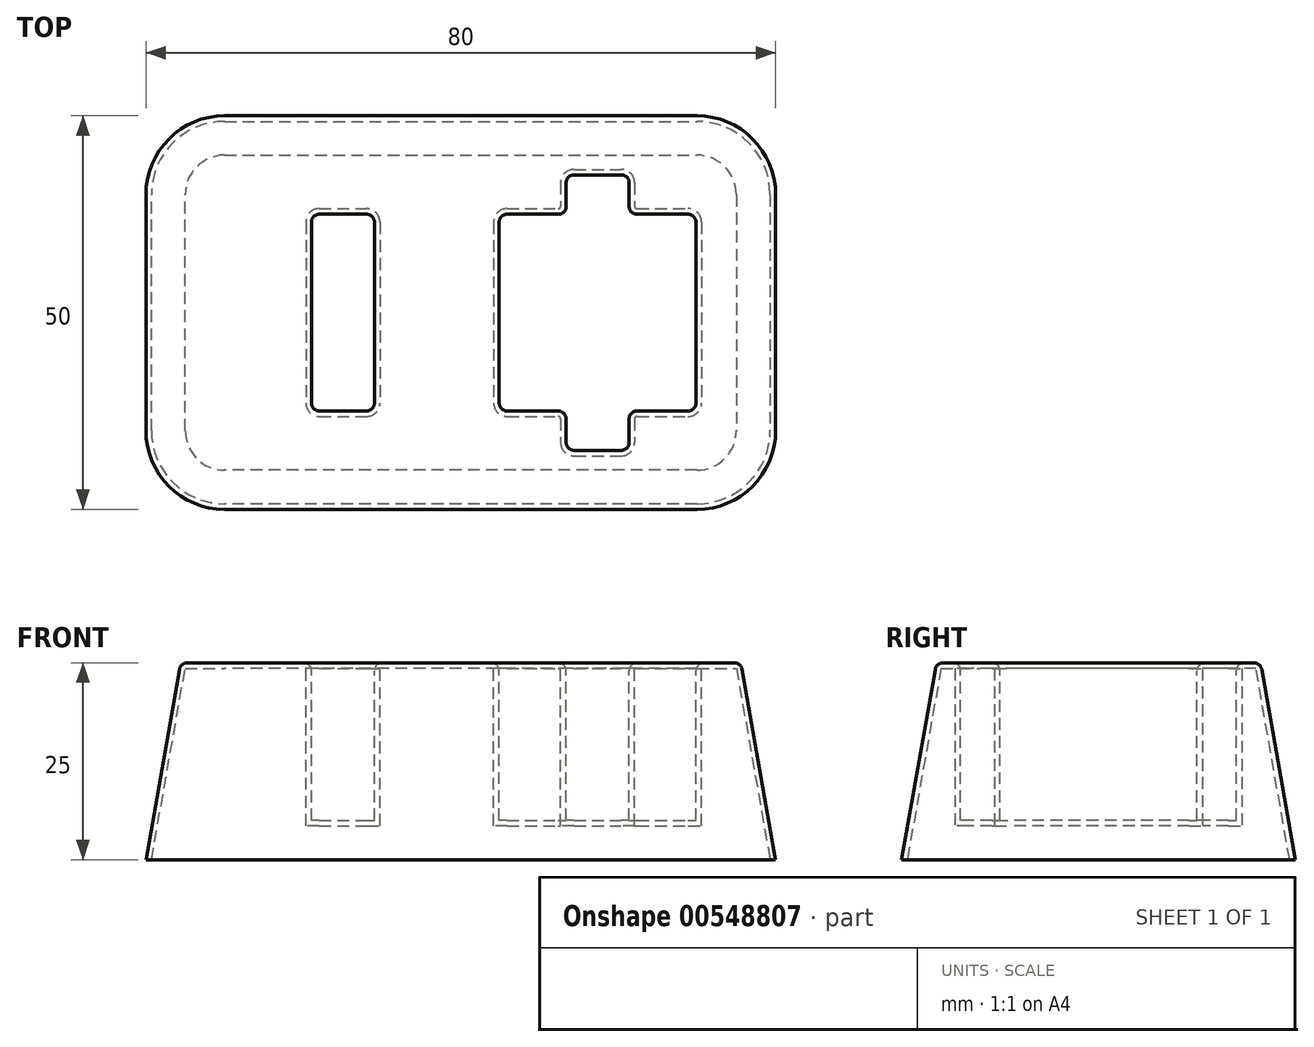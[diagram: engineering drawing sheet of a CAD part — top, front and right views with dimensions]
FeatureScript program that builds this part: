
annotation { "Feature Type Name" : "Feature", "Feature Type Description" : "" }
export const myFeature = defineFeature(function(context is Context, id is Id, definition is map)
    precondition{}
    {
        {
            var Q0;
            Q0=qCreatedBy(makeId("Top.planeOp"),FACE);
            var sketch = newSketch(context, id + "F0", { "sketchPlane" : qUnion([Q0])});
            skLineSegment(sketch, "E0.bottom", {"start": v(30, 25) * mm, "end": v(-30, 25) * mm});
            skLineSegment(sketch, "E0.top", {"start": v(30, -25) * mm, "end": v(-30, -25) * mm});
            skLineSegment(sketch, "E0.left", {"start": v(40, 15) * mm, "end": v(40, -15) * mm});
            skLineSegment(sketch, "E0.right", {"start": v(-40, 15) * mm, "end": v(-40, -15) * mm});
            skPoint(sketch, "E0.middle", {"position": v(0, 0) * mm});
            skPoint(sketch, "E1.visualSharp", {"position": v(-40, 25) * mm});
            skArc(sketch, "E1.filletArc", {"start": v(-30, 25) * mm, "mid": v(-37.07, 22.07) * mm, "end": v(-40, 15) * mm});
            skPoint(sketch, "E2.visualSharp", {"position": v(40, 25) * mm});
            skArc(sketch, "E2.filletArc", {"start": v(40, 15) * mm, "mid": v(37.07, 22.07) * mm, "end": v(30, 25) * mm});
            skPoint(sketch, "E3.visualSharp", {"position": v(40, -25) * mm});
            skArc(sketch, "E3.filletArc", {"start": v(30, -25) * mm, "mid": v(37.07, -22.07) * mm, "end": v(40, -15) * mm});
            skPoint(sketch, "E4.visualSharp", {"position": v(-40, -25) * mm});
            skArc(sketch, "E4.filletArc", {"start": v(-40, -15) * mm, "mid": v(-37.07, -22.07) * mm, "end": v(-30, -25) * mm});
            skSolve(sketch);
        }
        {
            var Q0;
            Q0 = qSketchRegion(id + "F0", true);
            extrude(context, id + "F1", {"entities" : qUnion([Q0]), "depth" : 25 * mm, "offsetDistance" : 25 * mm, "hasDraft" : true, "draftAngle" : 10 * degree, "draftPullDirection" : true});
        }
        {
            var Q0;
            Q0=makeQuery(id+"F1.opExtrude","CAP_FACE",FACE,{"disambiguationData":[OSD([sQuery(id+"F0.wireOp",EDGE,"E0.bottom"),sQuery(id+"F0.wireOp",EDGE,"E0.top"),sQuery(id+"F0.wireOp",EDGE,"E0.left"),sQuery(id+"F0.wireOp",EDGE,"E0.right"),sQuery(id+"F0.wireOp",EDGE,"E1.filletArc"),sQuery(id+"F0.wireOp",EDGE,"E2.filletArc"),sQuery(id+"F0.wireOp",EDGE,"E3.filletArc"),sQuery(id+"F0.wireOp",EDGE,"E4.filletArc")])],"isStart":false});
            var sketch = newSketch(context, id + "F2", { "sketchPlane" : qUnion([Q0])});
            skLineSegment(sketch, "E5.bottom", {"start": v(14.38, 17.5) * mm, "end": v(20.38, 17.5) * mm});
            skLineSegment(sketch, "E5.top", {"start": v(14.38, -17.5) * mm, "end": v(20.38, -17.5) * mm});
            skLineSegment(sketch, "E5.left", {"start": v(13.38, 16.5) * mm, "end": v(13.38, 13.5) * mm});
            skLineSegment(sketch, "E5.right", {"start": v(21.38, 16.5) * mm, "end": v(21.38, 13.5) * mm});
            skPoint(sketch, "E5.middle", {"position": v(17.38, 0) * mm});
            skLineSegment(sketch, "E6.bottom", {"start": v(5.88, 12.5) * mm, "end": v(12.38, 12.5) * mm});
            skLineSegment(sketch, "E6.top", {"start": v(5.88, -12.5) * mm, "end": v(12.38, -12.5) * mm});
            skLineSegment(sketch, "E6.left", {"start": v(4.88, 11.5) * mm, "end": v(4.88, -11.5) * mm});
            skLineSegment(sketch, "E6.right", {"start": v(29.88, 11.5) * mm, "end": v(29.88, -11.5) * mm});
            skLineSegment(sketch, "E7.trimOffspring", {"start": v(22.38, 12.5) * mm, "end": v(28.88, 12.5) * mm});
            skLineSegment(sketch, "E8.trimOffspring", {"start": v(13.38, -13.5) * mm, "end": v(13.38, -16.5) * mm});
            skLineSegment(sketch, "E9.trimOffspring", {"start": v(21.38, -13.5) * mm, "end": v(21.38, -16.5) * mm});
            skLineSegment(sketch, "E10.trimOffspring", {"start": v(22.38, -12.5) * mm, "end": v(28.88, -12.5) * mm});
            skPoint(sketch, "E11.visualSharp", {"position": v(13.38, 17.5) * mm});
            skArc(sketch, "E11.filletArc", {"start": v(14.38, 17.5) * mm, "mid": v(13.68, 17.2) * mm, "end": v(13.38, 16.5) * mm});
            skPoint(sketch, "E12.visualSharp", {"position": v(13.38, 12.5) * mm});
            skArc(sketch, "E12.filletArc", {"start": v(12.38, 12.5) * mm, "mid": v(13.09, 12.8) * mm, "end": v(13.38, 13.5) * mm});
            skPoint(sketch, "E13.visualSharp", {"position": v(21.38, 17.5) * mm});
            skArc(sketch, "E13.filletArc", {"start": v(21.38, 16.5) * mm, "mid": v(21.09, 17.2) * mm, "end": v(20.38, 17.5) * mm});
            skPoint(sketch, "E14.visualSharp", {"position": v(21.38, 12.5) * mm});
            skArc(sketch, "E14.filletArc", {"start": v(21.38, 13.5) * mm, "mid": v(21.68, 12.8) * mm, "end": v(22.38, 12.5) * mm});
            skPoint(sketch, "E15.visualSharp", {"position": v(29.88, 12.5) * mm});
            skArc(sketch, "E15.filletArc", {"start": v(29.88, 11.5) * mm, "mid": v(29.59, 12.2) * mm, "end": v(28.88, 12.5) * mm});
            skPoint(sketch, "E16.visualSharp", {"position": v(29.88, -12.5) * mm});
            skArc(sketch, "E16.filletArc", {"start": v(28.88, -12.5) * mm, "mid": v(29.59, -12.2) * mm, "end": v(29.88, -11.5) * mm});
            skPoint(sketch, "E17.visualSharp", {"position": v(21.38, -12.5) * mm});
            skArc(sketch, "E17.filletArc", {"start": v(22.38, -12.5) * mm, "mid": v(21.68, -12.8) * mm, "end": v(21.38, -13.5) * mm});
            skPoint(sketch, "E18.visualSharp", {"position": v(21.38, -17.5) * mm});
            skArc(sketch, "E18.filletArc", {"start": v(20.38, -17.5) * mm, "mid": v(21.09, -17.2) * mm, "end": v(21.38, -16.5) * mm});
            skPoint(sketch, "E19.visualSharp", {"position": v(13.38, -17.5) * mm});
            skArc(sketch, "E19.filletArc", {"start": v(13.38, -16.5) * mm, "mid": v(13.68, -17.2) * mm, "end": v(14.38, -17.5) * mm});
            skPoint(sketch, "E20.visualSharp", {"position": v(13.38, -12.5) * mm});
            skArc(sketch, "E20.filletArc", {"start": v(13.38, -13.5) * mm, "mid": v(13.09, -12.8) * mm, "end": v(12.38, -12.5) * mm});
            skPoint(sketch, "E21.visualSharp", {"position": v(4.88, -12.5) * mm});
            skArc(sketch, "E21.filletArc", {"start": v(4.88, -11.5) * mm, "mid": v(5.18, -12.2) * mm, "end": v(5.88, -12.5) * mm});
            skPoint(sketch, "E22.visualSharp", {"position": v(4.88, 12.5) * mm});
            skArc(sketch, "E22.filletArc", {"start": v(5.88, 12.5) * mm, "mid": v(5.18, 12.2) * mm, "end": v(4.88, 11.5) * mm});
            skSolve(sketch);
        }
        {
            var Q0;
            Q0=makeQuery(id+"F2.imprint","IMPRINT",FACE,{"disambiguationData":[TD([[makeQuery(id+"F2.imprint","IMPRINT",EDGE,{"derivedFrom":sQuery(id+"F2.wireOp",EDGE,"E5.bottom")}),1.0]])]});
            var sketch = newSketch(context, id + "F3", { "sketchPlane" : qUnion([Q0])});
            skLineSegment(sketch, "E23.bottom", {"start": v(-17.97, 12.5) * mm, "end": v(-11.97, 12.5) * mm});
            skLineSegment(sketch, "E23.top", {"start": v(-17.97, -12.5) * mm, "end": v(-11.97, -12.5) * mm});
            skLineSegment(sketch, "E23.left", {"start": v(-18.97, 11.5) * mm, "end": v(-18.97, -11.5) * mm});
            skLineSegment(sketch, "E23.right", {"start": v(-10.97, 11.5) * mm, "end": v(-10.97, -11.5) * mm});
            skPoint(sketch, "E23.middle", {"position": v(-14.97, 0) * mm});
            skPoint(sketch, "E24.visualSharp", {"position": v(-18.97, 12.5) * mm});
            skArc(sketch, "E24.filletArc", {"start": v(-17.97, 12.5) * mm, "mid": v(-18.68, 12.2) * mm, "end": v(-18.97, 11.5) * mm});
            skPoint(sketch, "E25.visualSharp", {"position": v(-10.97, 12.5) * mm});
            skArc(sketch, "E25.filletArc", {"start": v(-10.97, 11.5) * mm, "mid": v(-11.27, 12.2) * mm, "end": v(-11.97, 12.5) * mm});
            skPoint(sketch, "E26.visualSharp", {"position": v(-18.97, -12.5) * mm});
            skArc(sketch, "E26.filletArc", {"start": v(-18.97, -11.5) * mm, "mid": v(-18.68, -12.2) * mm, "end": v(-17.97, -12.5) * mm});
            skPoint(sketch, "E27.visualSharp", {"position": v(-10.97, -12.5) * mm});
            skArc(sketch, "E27.filletArc", {"start": v(-11.97, -12.5) * mm, "mid": v(-11.27, -12.2) * mm, "end": v(-10.97, -11.5) * mm});
            skSolve(sketch);
        }
        {
            var Q0;
            Q0 = qSketchRegion(id + "F2", true);
            extrude(context, id + "F4", {"entities" : qUnion([Q0]), "operationType" : NewBodyOperationType.REMOVE, "oppositeDirection" : true, "depth" : 20 * mm, "offsetDistance" : 25 * mm});
        }
        {
            var Q0;
            Q0 = qSketchRegion(id + "F3", true);
            extrude(context, id + "F5", {"entities" : qUnion([Q0]), "operationType" : NewBodyOperationType.REMOVE, "oppositeDirection" : true, "depth" : 20 * mm, "offsetDistance" : 25 * mm});
        }
        {
            var Q0;
            Q0=makeQuery(id+"F1.opExtrude","CAP_FACE",FACE,{"disambiguationData":[OSD([sQuery(id+"F0.wireOp",EDGE,"E0.bottom"),sQuery(id+"F0.wireOp",EDGE,"E0.top"),sQuery(id+"F0.wireOp",EDGE,"E0.left"),sQuery(id+"F0.wireOp",EDGE,"E0.right"),sQuery(id+"F0.wireOp",EDGE,"E1.filletArc"),sQuery(id+"F0.wireOp",EDGE,"E2.filletArc"),sQuery(id+"F0.wireOp",EDGE,"E3.filletArc"),sQuery(id+"F0.wireOp",EDGE,"E4.filletArc")])],"isStart":true});
            shell(context, id + "F6", {"entities" : qUnion([Q0]), "thickness" : .7 * mm});
        }
        {
            var Q0;
            Q0=makeQuery(id+"F1.opExtrude","CAP_FACE",FACE,{"disambiguationData":[OSD([sQuery(id+"F0.wireOp",EDGE,"E0.bottom"),sQuery(id+"F0.wireOp",EDGE,"E0.top"),sQuery(id+"F0.wireOp",EDGE,"E0.left"),sQuery(id+"F0.wireOp",EDGE,"E0.right"),sQuery(id+"F0.wireOp",EDGE,"E1.filletArc"),sQuery(id+"F0.wireOp",EDGE,"E2.filletArc"),sQuery(id+"F0.wireOp",EDGE,"E3.filletArc"),sQuery(id+"F0.wireOp",EDGE,"E4.filletArc")])],"isStart":false});
            fillet(context, id + "F7", {"entities" : qUnion([Q0]), "radius" : 1 * mm, "tangentPropagation" : true, "allowEdgeOverflow" : false});
        }
    });
